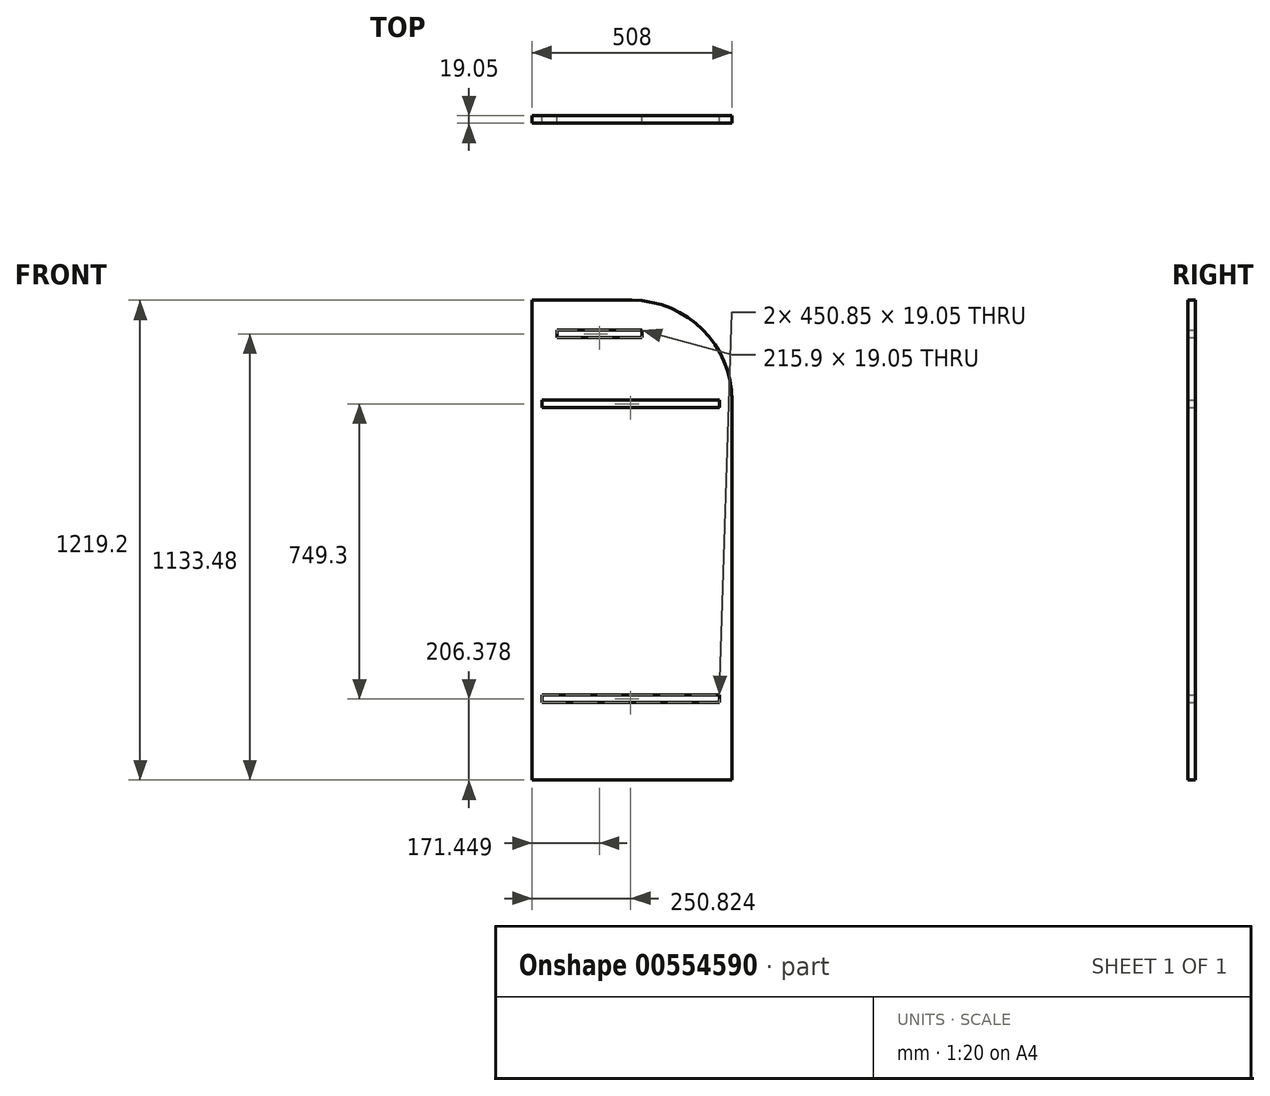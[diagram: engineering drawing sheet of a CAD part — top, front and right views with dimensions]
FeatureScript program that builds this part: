
annotation { "Feature Type Name" : "Feature", "Feature Type Description" : "" }
export const myFeature = defineFeature(function(context is Context, id is Id, definition is map)
    precondition{}
    {
        {
            var Q0;
            Q0=qCreatedBy(makeId("Front.planeOp"),FACE);
            var sketch = newSketch(context, id + "F0", { "sketchPlane" : qUnion([Q0])});
            skLineSegment(sketch, "E0", {"start": v(-615.72, -361.28) * mm, "end": v(-107.72, -361.28) * mm});
            skLineSegment(sketch, "E1", {"start": v(-107.72, -361.28) * mm, "end": v(-107.72, 603.92) * mm});
            skLineSegment(sketch, "E2", {"start": v(-361.72, 857.92) * mm, "end": v(-615.72, 857.92) * mm});
            skLineSegment(sketch, "E3", {"start": v(-615.72, 857.92) * mm, "end": v(-615.72, -361.28) * mm});
            skPoint(sketch, "E4.visualSharp", {"position": v(-107.72, 857.92) * mm});
            skArc(sketch, "E4.filletArc", {"start": v(-107.72, 603.92) * mm, "mid": v(-182.12, 783.53) * mm, "end": v(-361.72, 857.92) * mm});
            skLineSegment(sketch, "E5", {"start": v(-552.22, 781.72) * mm, "end": v(-552.22, 762.67) * mm});
            skLineSegment(sketch, "E6", {"start": v(-552.22, 762.67) * mm, "end": v(-336.32, 762.67) * mm});
            skLineSegment(sketch, "E7", {"start": v(-552.22, 781.72) * mm, "end": v(-336.32, 781.72) * mm});
            skLineSegment(sketch, "E8", {"start": v(-336.32, 781.72) * mm, "end": v(-336.32, 762.67) * mm});
            skLineSegment(sketch, "E9", {"start": v(-590.32, 603.92) * mm, "end": v(-139.47, 603.92) * mm});
            skLineSegment(sketch, "E10", {"start": v(-590.32, 603.92) * mm, "end": v(-590.32, 584.87) * mm});
            skLineSegment(sketch, "E11", {"start": v(-590.32, 584.87) * mm, "end": v(-139.47, 584.87) * mm});
            skLineSegment(sketch, "E12", {"start": v(-139.47, 584.87) * mm, "end": v(-139.47, 603.92) * mm});
            skLineSegment(sketch, "E13", {"start": v(-590.32, -145.38) * mm, "end": v(-139.47, -145.38) * mm});
            skLineSegment(sketch, "E14", {"start": v(-590.32, -145.38) * mm, "end": v(-590.32, -164.43) * mm});
            skLineSegment(sketch, "E15", {"start": v(-590.32, -164.43) * mm, "end": v(-139.47, -164.43) * mm});
            skLineSegment(sketch, "E16", {"start": v(-139.47, -164.43) * mm, "end": v(-139.47, -145.38) * mm});
            skSolve(sketch);
        }
        {
            var Q0;
            Q0 = qSketchRegion(id + "F0", true);
            extrude(context, id + "F1", {"entities" : qUnion([Q0]), "depth" : 19.05 * mm, "offsetDistance" : 25.4 * mm});
        }
    });
